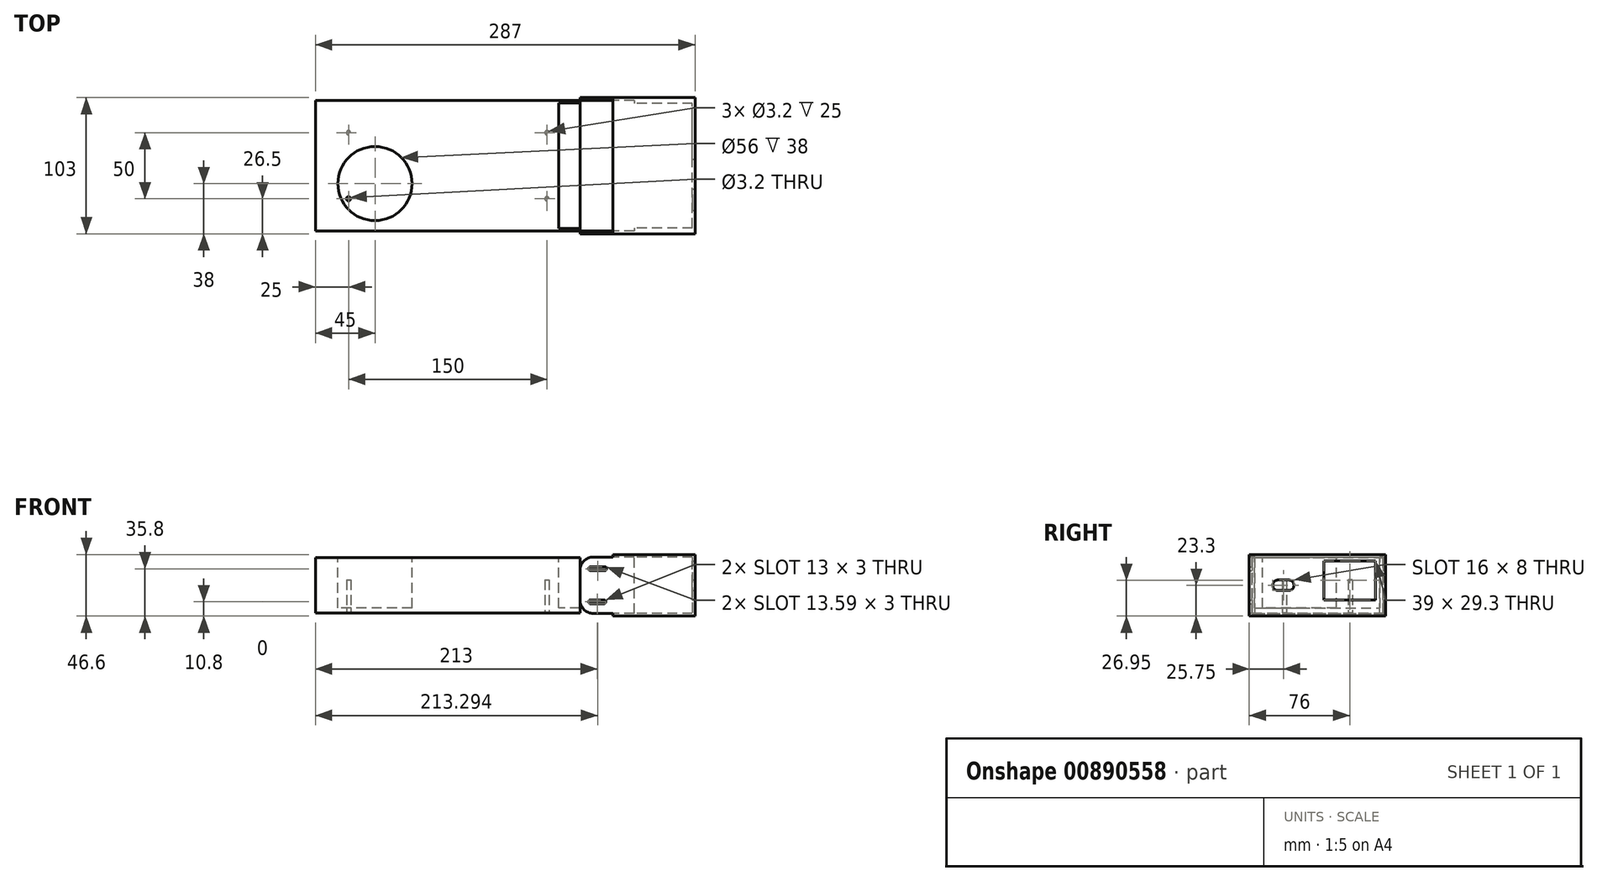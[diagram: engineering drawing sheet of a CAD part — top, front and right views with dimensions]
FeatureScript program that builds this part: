
annotation { "Feature Type Name" : "Feature", "Feature Type Description" : "" }
export const myFeature = defineFeature(function(context is Context, id is Id, definition is map)
    precondition{}
    {
        {
            var Q0;
            Q0=qCreatedBy(makeId("Top.planeOp"),FACE);
            var sketch = newSketch(context, id + "F0", { "sketchPlane" : qUnion([Q0])});
            skLineSegment(sketch, "E0.bottom", {"start": v(100, -49.5) * mm, "end": v(-100, -49.5) * mm});
            skLineSegment(sketch, "E0.top", {"start": v(100, 49.5) * mm, "end": v(-100, 49.5) * mm});
            skLineSegment(sketch, "E0.left", {"start": v(100, -49.5) * mm, "end": v(100, 49.5) * mm});
            skLineSegment(sketch, "E0.right", {"start": v(-100, -49.5) * mm, "end": v(-100, 49.5) * mm});
            skPoint(sketch, "E0.middle", {"position": v(0, 0) * mm});
            skSolve(sketch);
        }
        {
            var Q0;
            Q0 = qSketchRegion(id + "F0", true);
            extrude(context, id + "F1", {"entities" : qUnion([Q0]), "depth" : 41.8 * mm, "offsetDistance" : 25 * mm});
        }
        {
            var Q0;
            Q0=makeQuery(id+"F1.opExtrude","CAP_FACE",FACE,{"disambiguationData":[OSD([sQuery(id+"F0.wireOp",EDGE,"E0.bottom"),sQuery(id+"F0.wireOp",EDGE,"E0.top"),sQuery(id+"F0.wireOp",EDGE,"E0.left"),sQuery(id+"F0.wireOp",EDGE,"E0.right")])],"isStart":false});
            var sketch = newSketch(context, id + "F2", { "sketchPlane" : qUnion([Q0])});
            skLineSegment(sketch, "E1.bottom", {"start": v(100, 47.5) * mm, "end": v(84, 47.5) * mm});
            skLineSegment(sketch, "E1.top", {"start": v(100, -47.5) * mm, "end": v(84, -47.5) * mm});
            skLineSegment(sketch, "E1.left", {"start": v(100, 47.5) * mm, "end": v(100, -47.5) * mm});
            skLineSegment(sketch, "E1.right", {"start": v(84, 47.5) * mm, "end": v(84, -47.5) * mm});
            skCircle(sketch, "E2", {"center": v(-55, -13.5) * mm, "radius": 28 * mm});
            skSolve(sketch);
        }
        {
            var Q0;
            Q0 = qSketchRegion(id + "F2", true);
            extrude(context, id + "F3", {"entities" : qUnion([Q0]), "operationType" : NewBodyOperationType.REMOVE, "oppositeDirection" : true, "depth" : 38 * mm, "offsetDistance" : 25 * mm});
        }
        {
            var Q0;
            Q0=makeQuery(id+"F1.opExtrude","CAP_FACE",FACE,{"disambiguationData":[OSD([sQuery(id+"F0.wireOp",EDGE,"E0.bottom"),sQuery(id+"F0.wireOp",EDGE,"E0.top"),sQuery(id+"F0.wireOp",EDGE,"E0.left"),sQuery(id+"F0.wireOp",EDGE,"E0.right")])],"isStart":true});
            var sketch = newSketch(context, id + "F4", { "sketchPlane" : qUnion([Q0])});
            skCircle(sketch, "E3", {"center": v(-75, 25) * mm, "radius": 1.6 * mm});
            skCircle(sketch, "E4.MirrorC", {"center": v(75, 25) * mm, "radius": 1.6 * mm});
            skCircle(sketch, "E5.MirrorC", {"center": v(-75, -25) * mm, "radius": 1.6 * mm});
            skCircle(sketch, "E6.MirrorC", {"center": v(75, -25) * mm, "radius": 1.6 * mm});
            skSolve(sketch);
        }
        {
            var Q0;
            Q0 = qSketchRegion(id + "F4", true);
            extrude(context, id + "F5", {"entities" : qUnion([Q0]), "operationType" : NewBodyOperationType.REMOVE, "oppositeDirection" : true, "depth" : 25 * mm, "offsetDistance" : 25 * mm});
        }
        {
            var Q0;
            Q0=makeQuery(id+"F1.opExtrude","SWEPT_FACE",FACE,{"disambiguationData":[OSD([sQuery(id+"F0.wireOp",EDGE,"E0.left")])]});
            cPlane(context, id + "F6", {"entities" : qUnion([Q0]), "cplaneType" : CPlaneType.OFFSET, "offset" : 25 * mm, "width" : 150 * mm, "height" : 150 * mm});
        }
        {
            var Q0;
            Q0=qCreatedBy(id+"F6.planeOp",FACE);
            var sketch = newSketch(context, id + "F7", { "sketchPlane" : qUnion([Q0])});
            skLineSegment(sketch, "E7.bottom", {"start": v(-47.1, 42.2) * mm, "end": v(47.1, 42.2) * mm});
            skLineSegment(sketch, "E7.top", {"start": v(-47.1, -0.4) * mm, "end": v(47.1, -0.4) * mm});
            skLineSegment(sketch, "E7.left", {"start": v(-47.1, 42.2) * mm, "end": v(-47.1, -0.4) * mm});
            skLineSegment(sketch, "E7.right", {"start": v(47.1, 42.2) * mm, "end": v(47.1, -0.4) * mm});
            skLineSegment(sketch, "E8.bottom", {"start": v(-51.5, 44.2) * mm, "end": v(51.5, 44.2) * mm});
            skLineSegment(sketch, "E8.top", {"start": v(-51.5, -2.4) * mm, "end": v(51.5, -2.4) * mm});
            skLineSegment(sketch, "E8.left", {"start": v(-51.5, 44.2) * mm, "end": v(-51.5, -2.4) * mm});
            skLineSegment(sketch, "E8.right", {"start": v(51.5, 44.2) * mm, "end": v(51.5, -2.4) * mm});
            skSolve(sketch);
        }
        {
            var Q0;
            Q0 = qSketchRegion(id + "F7", true);
            extrude(context, id + "F8", {"entities" : qUnion([Q0]), "depth" : 60 * mm, "offsetDistance" : 25 * mm});
        }
        {
            var Q0;
            Q0=makeQuery(id+"F8.opExtrude","CAP_FACE",FACE,{"disambiguationData":[OSD([sQuery(id+"F7.wireOp",EDGE,"E7.bottom"),sQuery(id+"F7.wireOp",EDGE,"E7.top"),sQuery(id+"F7.wireOp",EDGE,"E7.left"),sQuery(id+"F7.wireOp",EDGE,"E7.right"),sQuery(id+"F7.wireOp",EDGE,"E8.bottom"),sQuery(id+"F7.wireOp",EDGE,"E8.top"),sQuery(id+"F7.wireOp",EDGE,"E8.left"),sQuery(id+"F7.wireOp",EDGE,"E8.right")])],"isStart":false});
            var sketch = newSketch(context, id + "F9", { "sketchPlane" : qUnion([Q0])});
            skSolve(sketch);
        }
        {
            var Q0;
            Q0=makeQuery(id+"F9.imprint","IMPRINT",FACE,{"disambiguationData":[TD([[makeQuery(id+"F9.imprint","IMPRINT",EDGE,{"derivedFrom":makeQuery(id+"F8.opExtrude","CAP_EDGE",EDGE,{"disambiguationData":[OSD([sQuery(id+"F7.wireOp",EDGE,"E7.bottom")])],"isStart":false})}),1.0]])]});
            var Q1;
            Q1=makeQuery(id+"F9.imprint","IMPRINT",FACE,{"disambiguationData":[TD([[makeQuery(id+"F9.imprint","IMPRINT",EDGE,{"derivedFrom":makeQuery(id+"F8.opExtrude","CAP_EDGE",EDGE,{"disambiguationData":[OSD([sQuery(id+"F7.wireOp",EDGE,"E7.bottom")])],"isStart":false})}),-1.0]])]});
            extrude(context, id + "F10", {"entities" : qUnion([Q0, Q1]), "operationType" : NewBodyOperationType.ADD, "depth" : 2 * mm, "offsetDistance" : 25 * mm});
        }
        {
            var Q0;
            Q0=makeQuery(id+"F10.opExtrude","CAP_FACE",FACE,{"disambiguationData":[OSD([sQuery(id+"F7.wireOp",EDGE,"E8.bottom"),sQuery(id+"F7.wireOp",EDGE,"E8.top"),sQuery(id+"F7.wireOp",EDGE,"E8.left"),sQuery(id+"F7.wireOp",EDGE,"E8.right")])],"isStart":false});
            var sketch = newSketch(context, id + "F11", { "sketchPlane" : qUnion([Q0])});
            skLineSegment(sketch, "E9.bottom", {"start": v(44, 9.9) * mm, "end": v(5, 9.9) * mm});
            skLineSegment(sketch, "E9.top", {"start": v(44, 39.2) * mm, "end": v(5, 39.2) * mm});
            skLineSegment(sketch, "E9.left", {"start": v(5, 39.2) * mm, "end": v(5, 9.9) * mm});
            skLineSegment(sketch, "E9.right", {"start": v(44, 39.2) * mm, "end": v(44, 9.9) * mm});
            skLineSegment(sketch, "E10", {"start": v(-29.75, 20.9) * mm, "end": v(-21.75, 20.9) * mm, "construction": true});
            skLineSegment(sketch, "E11", {"start": v(0, 44.2) * mm, "end": v(0, -2.4) * mm, "construction": true});
            skLineSegment(sketch, "E12", {"start": v(0, 44.2) * mm, "end": v(-51.5, 44.2) * mm, "construction": true});
            skPoint(sketch, "E13", {"position": v(-25.75, 20.9) * mm});
            skPoint(sketch, "E13.positionSnap0", {"position": v(0, 20.9) * mm});
            skPoint(sketch, "E13.positionSnap1", {"position": v(-25.75, 44.2) * mm});
            skArc(sketch, "E14.0.startCap", {"start": v(-29.75, 16.9) * mm, "mid": v(-33.75, 20.9) * mm, "end": v(-29.75, 24.9) * mm});
            skArc(sketch, "E14.0.endCap", {"start": v(-21.75, 24.9) * mm, "mid": v(-17.75, 20.9) * mm, "end": v(-21.75, 16.9) * mm});
            skLineSegment(sketch, "E14.0.left", {"start": v(-29.75, 24.9) * mm, "end": v(-21.75, 24.9) * mm});
            skLineSegment(sketch, "E14.0.right", {"start": v(-29.75, 16.9) * mm, "end": v(-21.75, 16.9) * mm});
            skSolve(sketch);
        }
        {
            var Q0;
            Q0 = qSketchRegion(id + "F11", true);
            var Q1;
            Q1=makeQuery(id+"F10.opExtrude","CAP_FACE",FACE,{"disambiguationData":[OSD([sQuery(id+"F7.wireOp",EDGE,"E8.bottom"),sQuery(id+"F7.wireOp",EDGE,"E8.top"),sQuery(id+"F7.wireOp",EDGE,"E8.left"),sQuery(id+"F7.wireOp",EDGE,"E8.right")])],"isStart":true});
            extrude(context, id + "F12", {"entities" : qUnion([Q0]), "operationType" : NewBodyOperationType.REMOVE, "endBound" : BoundingType.UP_TO_SURFACE, "oppositeDirection" : true, "depth" : 25 * mm, "endBoundEntityFace" : qUnion([Q1]), "offsetDistance" : 25 * mm});
        }
        {
            var Q0;
            Q0=makeQuery(id+"F8.opExtrude","CAP_FACE",FACE,{"disambiguationData":[OSD([sQuery(id+"F7.wireOp",EDGE,"E7.bottom"),sQuery(id+"F7.wireOp",EDGE,"E7.top"),sQuery(id+"F7.wireOp",EDGE,"E7.left"),sQuery(id+"F7.wireOp",EDGE,"E7.right"),sQuery(id+"F7.wireOp",EDGE,"E8.bottom"),sQuery(id+"F7.wireOp",EDGE,"E8.top"),sQuery(id+"F7.wireOp",EDGE,"E8.left"),sQuery(id+"F7.wireOp",EDGE,"E8.right")])],"isStart":true});
            var sketch = newSketch(context, id + "F13", { "sketchPlane" : qUnion([Q0])});
            skPoint(sketch, "E15.oppositeSnap0", {"position": v(49.5, -4.1) * mm});
            skLineSegment(sketch, "E15.bottom", {"start": v(-49.5, -0.4) * mm, "end": v(49.5, -0.4) * mm});
            skLineSegment(sketch, "E15.top", {"start": v(-49.5, 42.2) * mm, "end": v(49.5, 42.2) * mm});
            skLineSegment(sketch, "E15.left", {"start": v(-49.5, -0.4) * mm, "end": v(-49.5, 42.2) * mm});
            skLineSegment(sketch, "E15.right", {"start": v(49.5, -0.4) * mm, "end": v(49.5, 42.2) * mm});
            skSolve(sketch);
        }
        {
            var Q0;
            Q0 = qSketchRegion(id + "F13", true);
            extrude(context, id + "F14", {"entities" : qUnion([Q0]), "operationType" : NewBodyOperationType.REMOVE, "oppositeDirection" : true, "depth" : 16 * mm, "offsetDistance" : 25 * mm});
        }
        {
            var Q0;
            Q0=makeQuery(id+"F8.opExtrude","CAP_FACE",FACE,{"disambiguationData":[OSD([sQuery(id+"F7.wireOp",EDGE,"E7.bottom"),sQuery(id+"F7.wireOp",EDGE,"E7.top"),sQuery(id+"F7.wireOp",EDGE,"E7.left"),sQuery(id+"F7.wireOp",EDGE,"E7.right"),sQuery(id+"F7.wireOp",EDGE,"E8.bottom"),sQuery(id+"F7.wireOp",EDGE,"E8.top"),sQuery(id+"F7.wireOp",EDGE,"E8.left"),sQuery(id+"F7.wireOp",EDGE,"E8.right")])],"isStart":true});
            var sketch = newSketch(context, id + "F15", { "sketchPlane" : qUnion([Q0])});
            skLineSegment(sketch, "E16.bottom", {"start": v(-49.5, 42.2) * mm, "end": v(-51.5, 42.2) * mm});
            skLineSegment(sketch, "E16.top", {"start": v(-49.5, -0.4) * mm, "end": v(-51.5, -0.4) * mm});
            skLineSegment(sketch, "E16.left", {"start": v(-49.5, 42.2) * mm, "end": v(-49.5, -0.4) * mm});
            skLineSegment(sketch, "E16.right", {"start": v(-51.5, 42.2) * mm, "end": v(-51.5, -0.4) * mm});
            skLineSegment(sketch, "E17.bottom", {"start": v(49.5, 42.2) * mm, "end": v(51.5, 42.2) * mm});
            skLineSegment(sketch, "E17.top", {"start": v(49.5, -0.4) * mm, "end": v(51.5, -0.4) * mm});
            skLineSegment(sketch, "E17.left", {"start": v(49.5, 42.2) * mm, "end": v(49.5, -0.4) * mm});
            skLineSegment(sketch, "E17.right", {"start": v(51.5, 42.2) * mm, "end": v(51.5, -0.4) * mm});
            skSolve(sketch);
        }
        {
            var Q0;
            Q0 = qSketchRegion(id + "F15", true);
            extrude(context, id + "F16", {"entities" : qUnion([Q0]), "operationType" : NewBodyOperationType.ADD, "depth" : 25 * mm, "offsetDistance" : 25 * mm});
        }
        {
            var Q0;
            Q0=makeQuery(id+"F16.opExtrude","CAP_EDGE",EDGE,{"disambiguationData":[OSD([sQuery(id+"F15.wireOp",EDGE,"E16.bottom")])],"isStart":false});
            var Q1;
            Q1=makeQuery(id+"F16.opExtrude","CAP_EDGE",EDGE,{"disambiguationData":[OSD([sQuery(id+"F15.wireOp",EDGE,"E16.top")])],"isStart":false});
            var Q2;
            Q2=makeQuery(id+"F16.opExtrude","CAP_EDGE",EDGE,{"disambiguationData":[OSD([sQuery(id+"F15.wireOp",EDGE,"E17.bottom")])],"isStart":false});
            var Q3;
            Q3=makeQuery(id+"F16.opExtrude","CAP_EDGE",EDGE,{"disambiguationData":[OSD([sQuery(id+"F15.wireOp",EDGE,"E17.top")])],"isStart":false});
            fillet(context, id + "F17", {"entities" : qUnion([Q0, Q1, Q2, Q3]), "radius" : 10 * mm, "tangentPropagation" : true, "allowEdgeOverflow" : false});
        }
        {
            var Q0;
            {var subQ0=sQuery(id+"F7.wireOp",EDGE,"E8.right");Q0=makeQuery(id+"F16.boolean.opBoolean","MERGE",FACE,{"derivedFrom":[makeQuery(id+"F10.boolean.opBoolean","MERGE",FACE,{"derivedFrom":[makeQuery(id+"F8.opExtrude","SWEPT_FACE",FACE,{"disambiguationData":[OSD([subQ0])]}),makeQuery(id+"F10.opExtrude","SWEPT_FACE",FACE,{"disambiguationData":[OSD([subQ0])]})]}),makeQuery(id+"F16.opExtrude","SWEPT_FACE",FACE,{"disambiguationData":[OSD([sQuery(id+"F15.wireOp",EDGE,"E16.right")])]})]});}
            var sketch = newSketch(context, id + "F18", { "sketchPlane" : qUnion([Q0])});
            skLineSegment(sketch, "E18", {"start": v(-118, 8.4) * mm, "end": v(-108, 8.4) * mm, "construction": true});
            skLineSegment(sketch, "E19", {"start": v(-118.59, 33.4) * mm, "end": v(-108, 33.4) * mm, "construction": true});
            skLineSegment(sketch, "E20", {"start": v(-187, 20.9) * mm, "end": v(-100, 20.9) * mm, "construction": true});
            skArc(sketch, "E21.0.startCap", {"start": v(-118.59, 31.9) * mm, "mid": v(-120.09, 33.4) * mm, "end": v(-118.59, 34.9) * mm});
            skArc(sketch, "E21.0.endCap", {"start": v(-108, 34.9) * mm, "mid": v(-106.5, 33.4) * mm, "end": v(-108, 31.9) * mm});
            skLineSegment(sketch, "E21.0.left", {"start": v(-118.59, 34.9) * mm, "end": v(-108, 34.9) * mm});
            skLineSegment(sketch, "E21.0.right", {"start": v(-118.59, 31.9) * mm, "end": v(-108, 31.9) * mm});
            skArc(sketch, "E21.1.startCap", {"start": v(-118, 6.9) * mm, "mid": v(-119.5, 8.4) * mm, "end": v(-118, 9.9) * mm});
            skArc(sketch, "E21.1.endCap", {"start": v(-108, 9.9) * mm, "mid": v(-106.5, 8.4) * mm, "end": v(-108, 6.9) * mm});
            skLineSegment(sketch, "E21.1.left", {"start": v(-118, 9.9) * mm, "end": v(-108, 9.9) * mm});
            skLineSegment(sketch, "E21.1.right", {"start": v(-118, 6.9) * mm, "end": v(-108, 6.9) * mm});
            skSolve(sketch);
        }
        {
            var Q0;
            Q0 = qSketchRegion(id + "F18", true);
            extrude(context, id + "F19", {"entities" : qUnion([Q0]), "operationType" : NewBodyOperationType.REMOVE, "endBound" : BoundingType.THROUGH_ALL, "oppositeDirection" : true, "depth" : 25 * mm, "offsetDistance" : 25 * mm});
        }
    });
